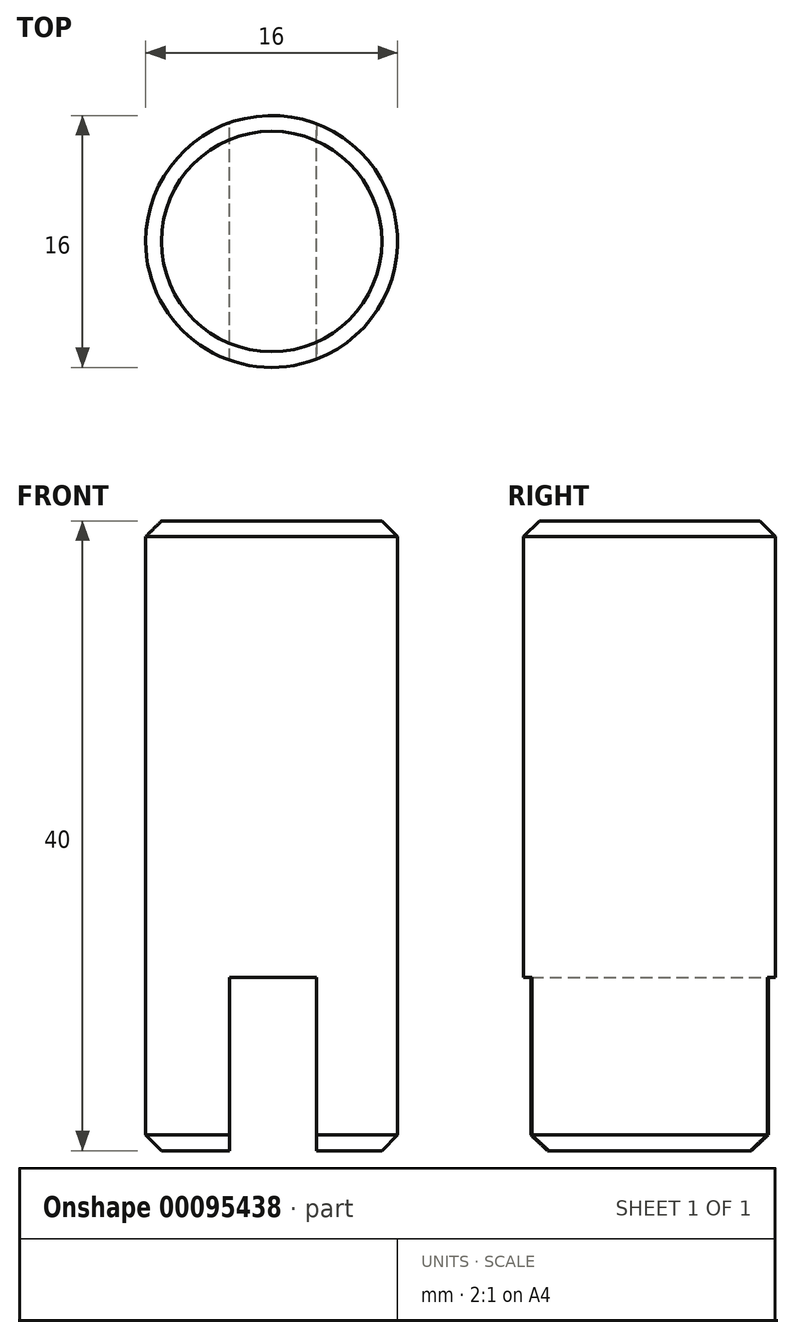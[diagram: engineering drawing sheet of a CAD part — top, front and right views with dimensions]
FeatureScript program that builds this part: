
annotation { "Feature Type Name" : "Feature", "Feature Type Description" : "" }
export const myFeature = defineFeature(function(context is Context, id is Id, definition is map)
    precondition{}
    {
        {
            var Q0;
            Q0=qCreatedBy(makeId("Front.planeOp"),FACE);
            var sketch = newSketch(context, id + "F0", { "sketchPlane" : qUnion([Q0])});
            skLineSegment(sketch, "E0.bottom", {"start": v(-8, 40) * mm, "end": v(0, 40) * mm});
            skLineSegment(sketch, "E0.top", {"start": v(-8, 0) * mm, "end": v(0, 0) * mm});
            skLineSegment(sketch, "E0.left", {"start": v(-8, 40) * mm, "end": v(-8, 0) * mm});
            skLineSegment(sketch, "E0.right", {"start": v(0, 40) * mm, "end": v(0, 0) * mm});
            skSolve(sketch);
        }
        {
            var Q0;
            Q0=makeQuery(id+"F0.imprint","IMPRINT",FACE,{"disambiguationData":[TD([[makeQuery(id+"F0.imprint","IMPRINT",EDGE,{"derivedFrom":sQuery(id+"F0.wireOp",EDGE,"E0.bottom")}),-1.0]])]});
            var Q1;
            Q1=sQuery(id+"F0.wireOp",EDGE,"E0.right");
            revolve(context, id + "F1", {"entities" : qUnion([Q0]), "axis" : qUnion([Q1]), "revolveType" : RevolveType.FULL});
        }
        {
            var Q0;
            Q0=qCreatedBy(makeId("Front.planeOp"),FACE);
            var sketch = newSketch(context, id + "F2", { "sketchPlane" : qUnion([Q0])});
            skLineSegment(sketch, "E1.bottom", {"start": v(-2.66, 11) * mm, "end": v(2.84, 11) * mm});
            skLineSegment(sketch, "E1.top", {"start": v(-2.66, 0) * mm, "end": v(2.84, 0) * mm});
            skLineSegment(sketch, "E1.left", {"start": v(-2.66, 11) * mm, "end": v(-2.66, 0) * mm});
            skLineSegment(sketch, "E1.right", {"start": v(2.84, 11) * mm, "end": v(2.84, 0) * mm});
            skSolve(sketch);
        }
        {
            var Q0;
            Q0 = qSketchRegion(id + "F2", true);
            extrude(context, id + "F3", {"entities" : qUnion([Q0]), "operationType" : NewBodyOperationType.REMOVE, "endBound" : BoundingType.SYMMETRIC, "depth" : 25 * mm});
        }
        {
            var Q0;
            Q0=makeQuery(id+"F1.opRevolve","SWEPT_EDGE",EDGE,{"disambiguationData":[OSD([sQuery(id+"F0.wireOp",EDGE,"E0.bottom"),sQuery(id+"F0.wireOp",EDGE,"E0.left")])]});
            var Q1;
            {var subQ0=sQuery(id+"F0.wireOp",EDGE,"E0.top");var subQ1=sQuery(id+"F0.wireOp",EDGE,"E0.left");Q1=makeQuery(id+"F3.boolean.opBoolean","SPLIT",EDGE,{"disambiguationData":[TD([makeQuery(id+"F3.opExtrude","SWEPT_FACE",FACE,{"disambiguationData":[OSD([sQuery(id+"F2.wireOp",EDGE,"E1.right")])]})])],"derivedFrom":makeQuery(id+"F1.opRevolve","SWEPT_EDGE",EDGE,{"disambiguationData":[OSD([subQ0,subQ1])]})});}
            var Q2;
            {var subQ0=sQuery(id+"F0.wireOp",EDGE,"E0.top");var subQ1=sQuery(id+"F0.wireOp",EDGE,"E0.left");Q2=makeQuery(id+"F3.boolean.opBoolean","SPLIT",EDGE,{"disambiguationData":[TD([makeQuery(id+"F3.opExtrude","SWEPT_FACE",FACE,{"disambiguationData":[OSD([sQuery(id+"F2.wireOp",EDGE,"E1.left")])]})])],"derivedFrom":makeQuery(id+"F1.opRevolve","SWEPT_EDGE",EDGE,{"disambiguationData":[OSD([subQ0,subQ1])]})});}
            chamfer(context, id + "F4", {"entities" : qUnion([Q0, Q1, Q2]), "width" : 1 * mm, "tangentPropagation" : true});
        }
    });
